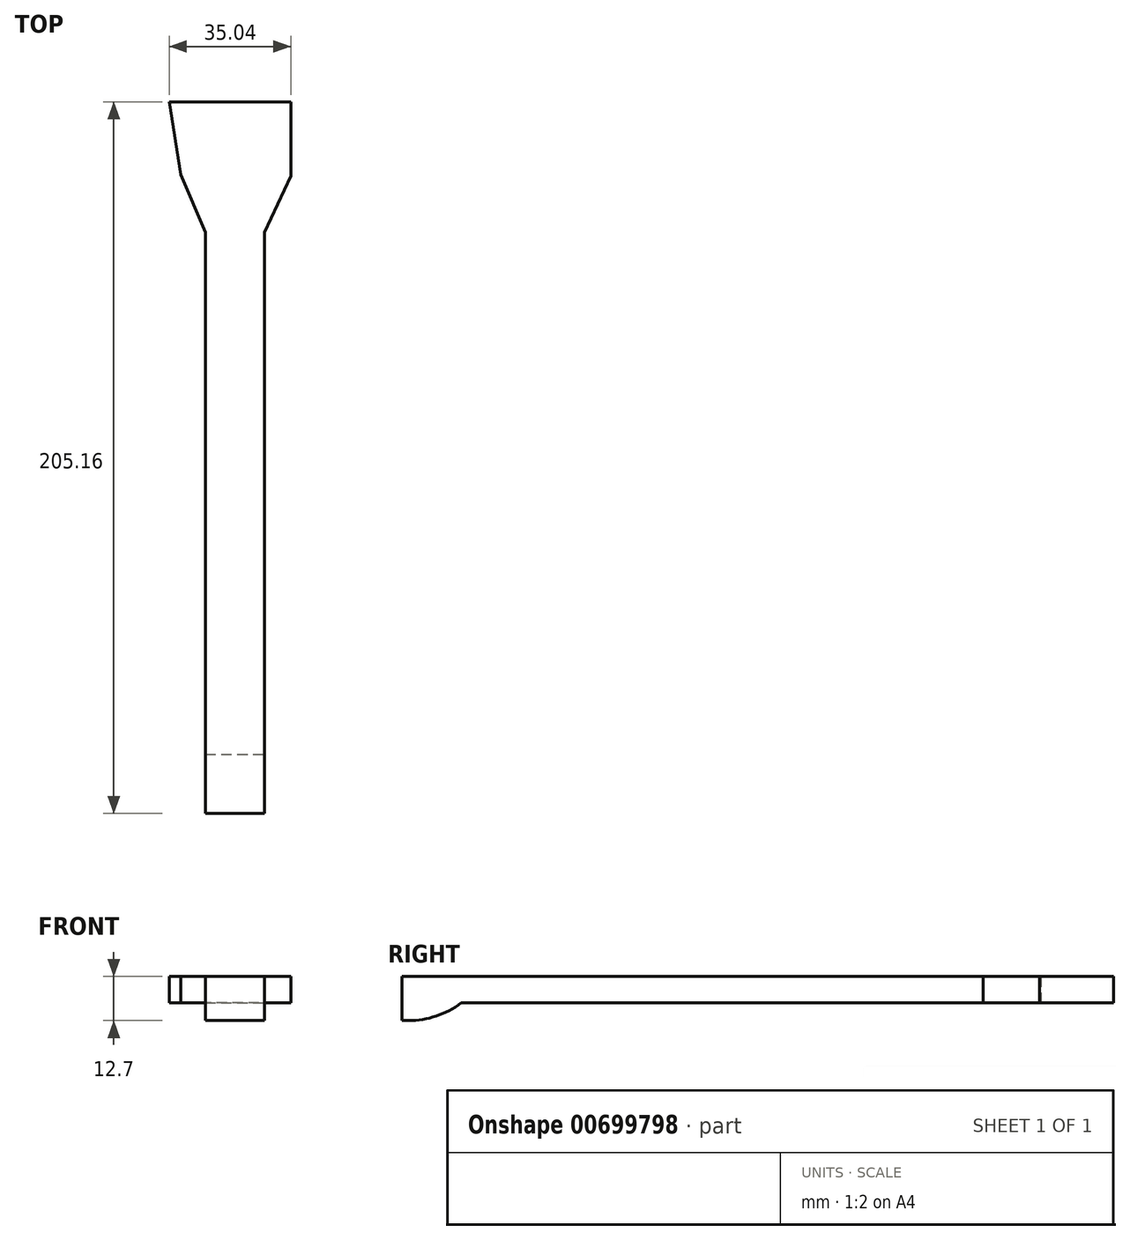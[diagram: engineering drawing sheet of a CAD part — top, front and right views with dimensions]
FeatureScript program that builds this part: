
annotation { "Feature Type Name" : "Feature", "Feature Type Description" : "" }
export const myFeature = defineFeature(function(context is Context, id is Id, definition is map)
    precondition{}
    {
        {
            var Q0;
            Q0=qCreatedBy(makeId("Top.planeOp"),FACE);
            var sketch = newSketch(context, id + "F0", { "sketchPlane" : qUnion([Q0])});
            skLineSegment(sketch, "E0.bottom", {"start": v(-161.04, -12.8) * mm, "end": v(-143.97, -12.8) * mm});
            skLineSegment(sketch, "E0.top", {"start": v(-161.04, 154.78) * mm, "end": v(-143.97, 154.78) * mm});
            skLineSegment(sketch, "E0.left", {"start": v(-161.04, -12.8) * mm, "end": v(-161.04, 154.78) * mm});
            skLineSegment(sketch, "E0.right", {"start": v(-143.97, -12.8) * mm, "end": v(-143.97, 154.78) * mm});
            skLineSegment(sketch, "E1", {"start": v(-161.04, 154.78) * mm, "end": v(-168.11, 171.42) * mm});
            skLineSegment(sketch, "E2", {"start": v(-143.97, 154.78) * mm, "end": v(-136.38, 170.98) * mm});
            skLineSegment(sketch, "E3", {"start": v(-136.38, 170.98) * mm, "end": v(-136.38, 192.36) * mm});
            skLineSegment(sketch, "E4", {"start": v(-136.38, 192.36) * mm, "end": v(-171.42, 192.36) * mm});
            skLineSegment(sketch, "E5", {"start": v(-168.11, 171.42) * mm, "end": v(-171.42, 192.36) * mm});
            skSolve(sketch);
        }
        {
            var Q0;
            Q0 = qSketchRegion(id + "F0", true);
            extrude(context, id + "F1", {"entities" : qUnion([Q0]), "depth" : 7.62 * mm, "offsetDistance" : 25.4 * mm});
        }
        {
            var Q0;
            Q0=makeQuery(id+"F1.opExtrude","CAP_FACE",FACE,{"disambiguationData":[OSD([sQuery(id+"F0.wireOp",EDGE,"E0.bottom"),sQuery(id+"F0.wireOp",EDGE,"E0.left"),sQuery(id+"F0.wireOp",EDGE,"E0.right"),sQuery(id+"F0.wireOp",EDGE,"E1"),sQuery(id+"F0.wireOp",EDGE,"E2"),sQuery(id+"F0.wireOp",EDGE,"E3"),sQuery(id+"F0.wireOp",EDGE,"E4"),sQuery(id+"F0.wireOp",EDGE,"E5")])],"isStart":true});
            var sketch = newSketch(context, id + "F2", { "sketchPlane" : qUnion([Q0])});
            skLineSegment(sketch, "E6.bottom", {"start": v(-161.04, 12.8) * mm, "end": v(-143.97, 12.8) * mm});
            skLineSegment(sketch, "E6.top", {"start": v(-161.04, -4.27) * mm, "end": v(-143.97, -4.27) * mm});
            skLineSegment(sketch, "E6.left", {"start": v(-161.04, 12.8) * mm, "end": v(-161.04, -4.27) * mm});
            skLineSegment(sketch, "E6.right", {"start": v(-143.97, 12.8) * mm, "end": v(-143.97, -4.27) * mm});
            skSolve(sketch);
        }
        {
            var Q0;
            Q0 = qSketchRegion(id + "F2", true);
            extrude(context, id + "F3", {"entities" : qUnion([Q0]), "operationType" : NewBodyOperationType.ADD, "depth" : 5.08 * mm, "offsetDistance" : 25.4 * mm});
        }
        {
            var Q0;
            Q0=makeQuery(id+"F3.opExtrude","CAP_EDGE",EDGE,{"disambiguationData":[OSD([sQuery(id+"F2.wireOp",EDGE,"E6.top")])],"isStart":false});
            fillet(context, id + "F4", {"entities" : qUnion([Q0]), "radius" : 25.14 * mm, "tangentPropagation" : true, "allowEdgeOverflow" : false});
        }
    });
